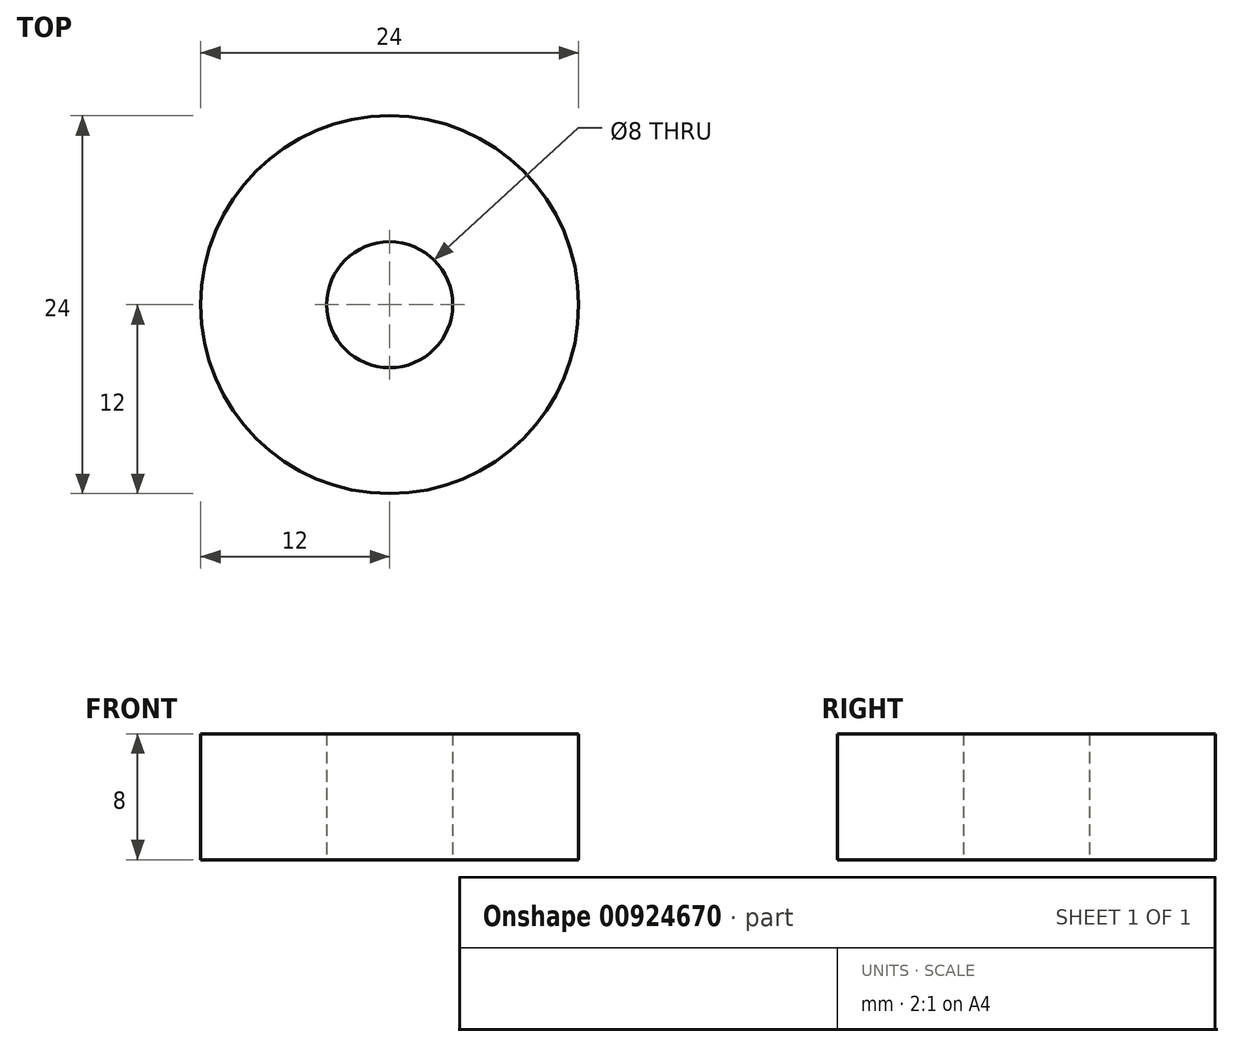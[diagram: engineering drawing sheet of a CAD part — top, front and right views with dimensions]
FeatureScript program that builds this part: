
annotation { "Feature Type Name" : "Feature", "Feature Type Description" : "" }
export const myFeature = defineFeature(function(context is Context, id is Id, definition is map)
    precondition{}
    {
        {
            var Q0;
            Q0=qCreatedBy(makeId("Top.planeOp"),FACE);
            var sketch = newSketch(context, id + "F0", { "sketchPlane" : qUnion([Q0])});
            skCircle(sketch, "E0", {"center": v(0, 0) * mm, "radius": 4 * mm});
            skCircle(sketch, "E1", {"center": v(0, 0) * mm, "radius": 12 * mm});
            skSolve(sketch);
        }
        {
            var Q0;
            Q0=makeQuery(id+"F0.imprint","IMPRINT",FACE,{"disambiguationData":[TD([[makeQuery(id+"F0.imprint","IMPRINT",EDGE,{"derivedFrom":sQuery(id+"F0.wireOp",EDGE,"E0")}),-1.0]])]});
            extrude(context, id + "F1", {"entities" : qUnion([Q0]), "depth" : 8 * mm, "offsetDistance" : 25 * mm});
        }
    });
